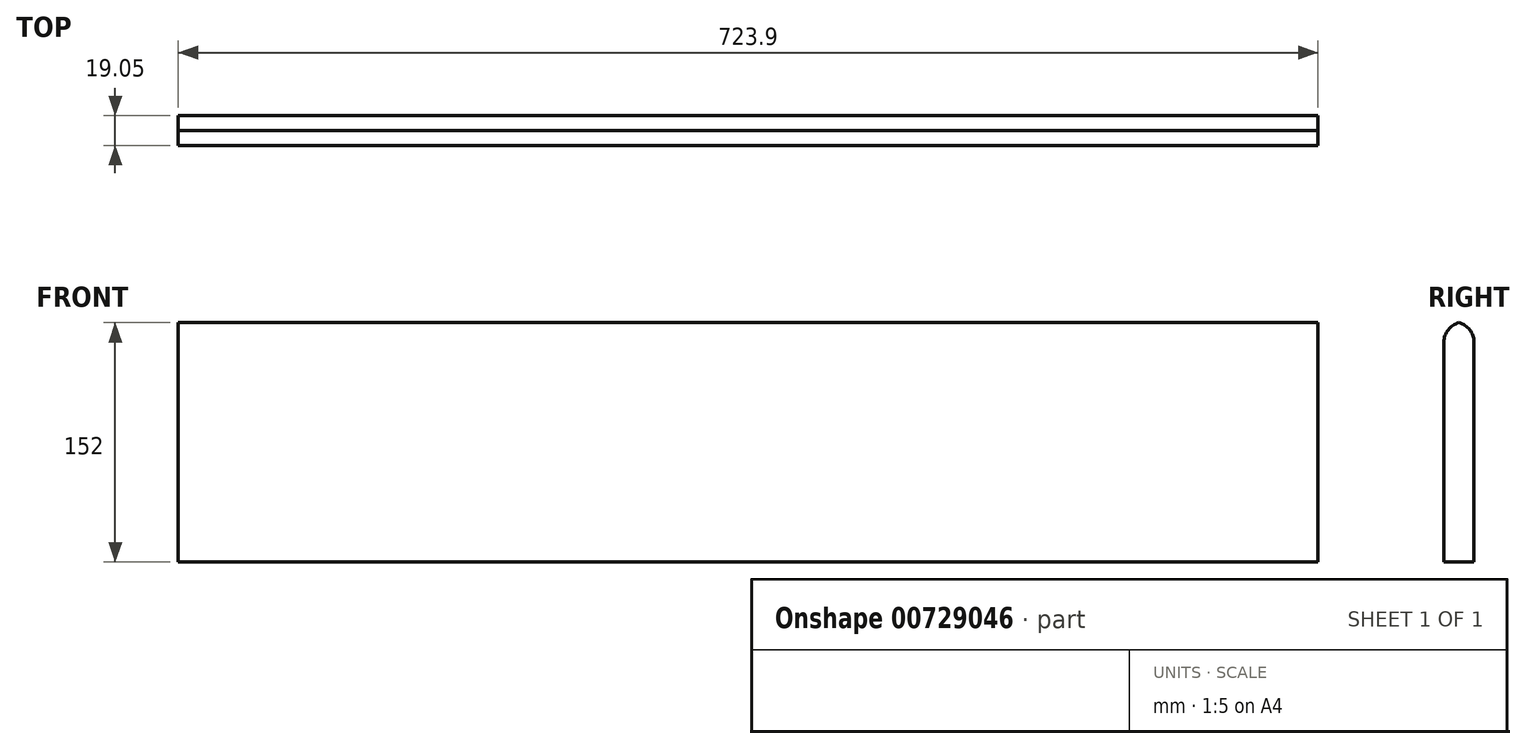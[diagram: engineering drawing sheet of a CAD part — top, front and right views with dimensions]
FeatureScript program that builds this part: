
annotation { "Feature Type Name" : "Feature", "Feature Type Description" : "" }
export const myFeature = defineFeature(function(context is Context, id is Id, definition is map)
    precondition{}
    {
        {
            var Q0;
            Q0=qCreatedBy(makeId("Front.planeOp"),FACE);
            var sketch = newSketch(context, id + "F0", { "sketchPlane" : qUnion([Q0])});
            skLineSegment(sketch, "E0.bottom", {"start": v(361.95, -76.2) * mm, "end": v(-361.95, -76.2) * mm});
            skLineSegment(sketch, "E0.top", {"start": v(361.95, 76.2) * mm, "end": v(-361.95, 76.2) * mm});
            skLineSegment(sketch, "E0.left", {"start": v(361.95, -76.2) * mm, "end": v(361.95, 76.2) * mm});
            skLineSegment(sketch, "E0.right", {"start": v(-361.95, -76.2) * mm, "end": v(-361.95, 76.2) * mm});
            skPoint(sketch, "E0.middle", {"position": v(0, 0) * mm});
            skSolve(sketch);
        }
        {
            var Q0;
            Q0 = qSketchRegion(id + "F0", true);
            extrude(context, id + "F1", {"entities" : qUnion([Q0]), "depth" : 19.05 * mm, "offsetDistance" : 25.4 * mm});
        }
        {
            var Q0;
            Q0=makeQuery(id+"F1.opExtrude","CAP_EDGE",EDGE,{"disambiguationData":[OSD([sQuery(id+"F0.wireOp",EDGE,"E0.top")])],"isStart":true});
            var Q1;
            Q1=makeQuery(id+"F1.opExtrude","CAP_EDGE",EDGE,{"disambiguationData":[OSD([sQuery(id+"F0.wireOp",EDGE,"E0.top")])],"isStart":false});
            fillet(context, id + "F2", {"entities" : qUnion([Q0, Q1]), "radius" : 12.7 * mm, "tangentPropagation" : true, "allowEdgeOverflow" : false});
        }
    });
